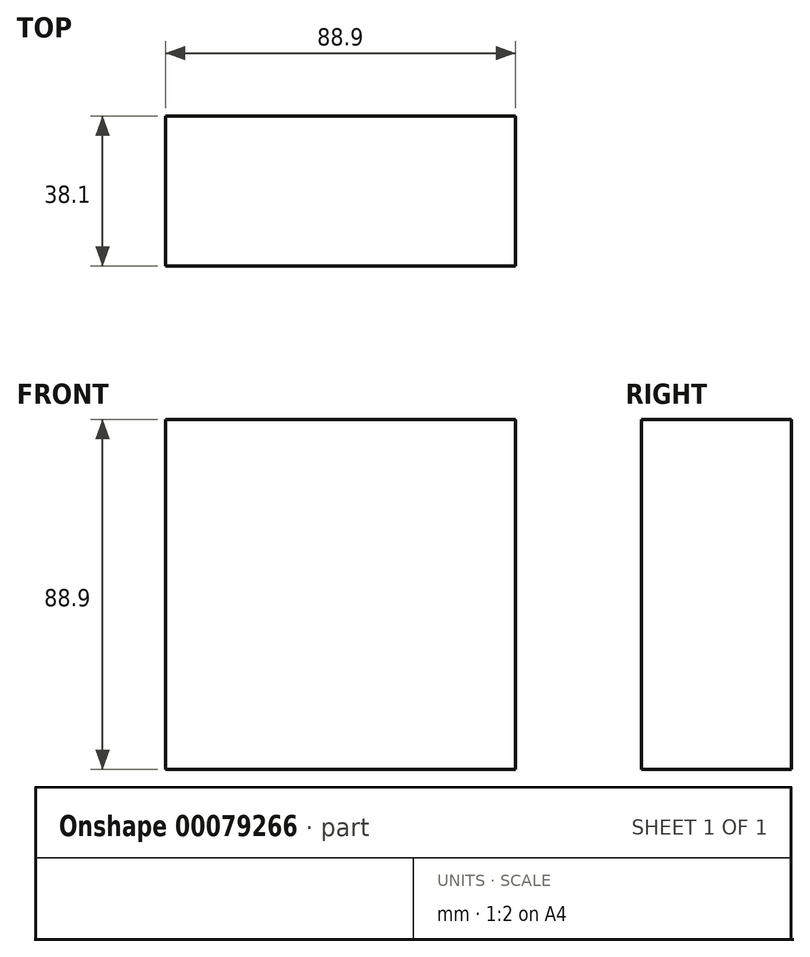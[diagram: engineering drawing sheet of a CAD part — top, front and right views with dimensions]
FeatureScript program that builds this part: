
annotation { "Feature Type Name" : "Feature", "Feature Type Description" : "" }
export const myFeature = defineFeature(function(context is Context, id is Id, definition is map)
    precondition{}
    {
        {
            var Q0;
            Q0=qCreatedBy(makeId("Right.planeOp"),FACE);
            var sketch = newSketch(context, id + "F0", { "sketchPlane" : qUnion([Q0])});
            skLineSegment(sketch, "E0.bottom", {"start": v(0, 0) * mm, "end": v(-38.1, 0) * mm});
            skLineSegment(sketch, "E0.top", {"start": v(0, 88.9) * mm, "end": v(-38.1, 88.9) * mm});
            skLineSegment(sketch, "E0.left", {"start": v(0, 0) * mm, "end": v(0, 88.9) * mm});
            skLineSegment(sketch, "E0.right", {"start": v(-38.1, 0) * mm, "end": v(-38.1, 88.9) * mm});
            skSolve(sketch);
        }
        {
            var Q0;
            Q0=makeQuery(id+"F0.imprint","IMPRINT",FACE,{"disambiguationData":[TD([[makeQuery(id+"F0.imprint","IMPRINT",EDGE,{"derivedFrom":sQuery(id+"F0.wireOp",EDGE,"E0.bottom")}),-1.0]])]});
            extrude(context, id + "F1", {"entities" : qUnion([Q0]), "depth" : 88.9 * mm});
        }
    });
